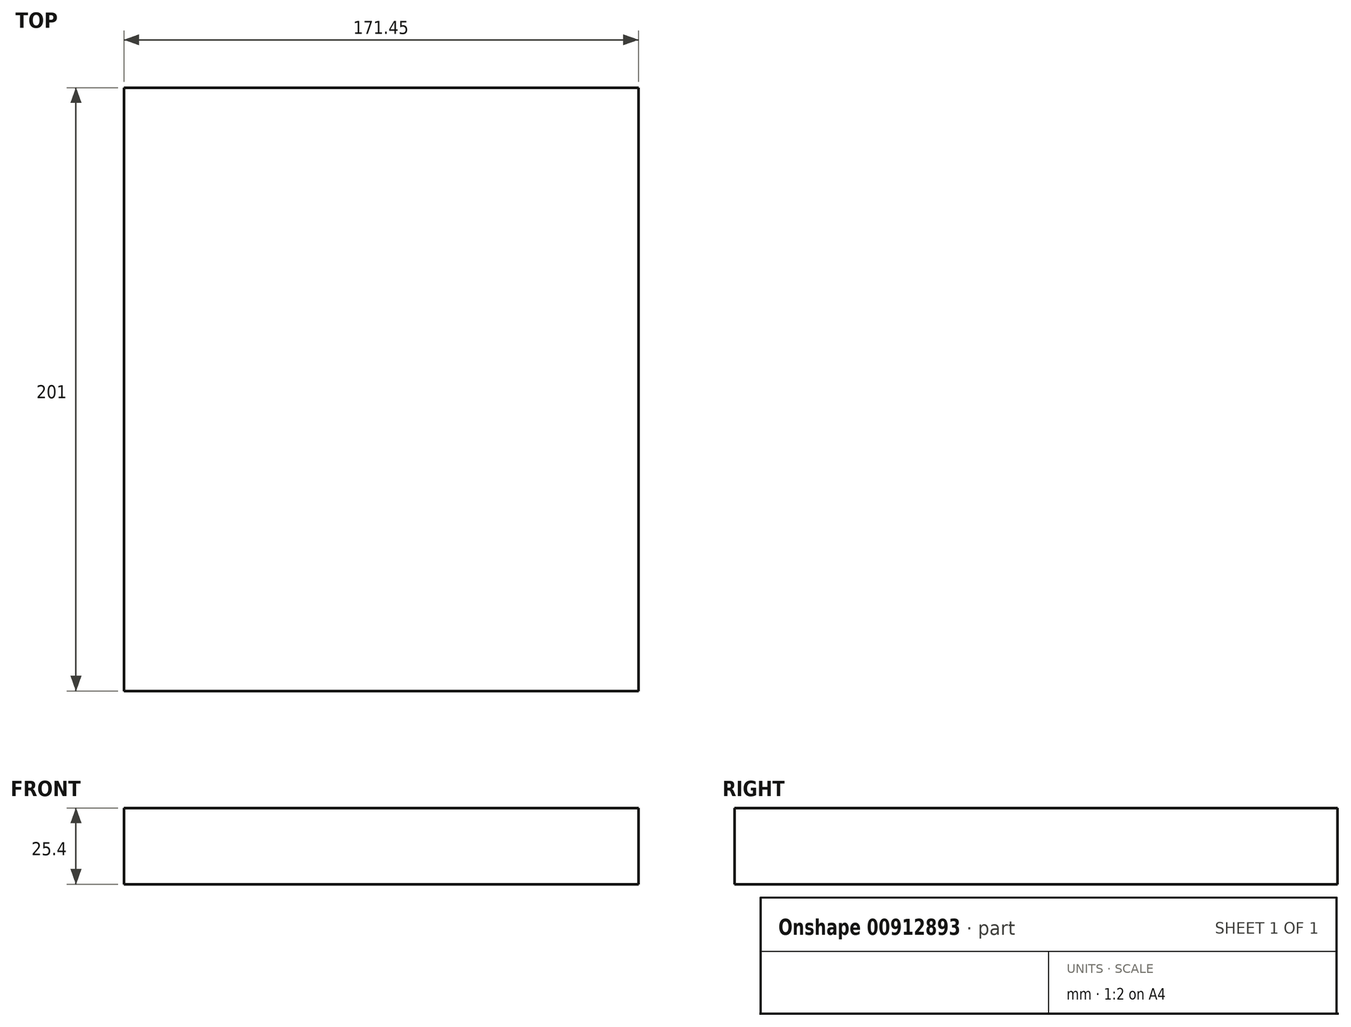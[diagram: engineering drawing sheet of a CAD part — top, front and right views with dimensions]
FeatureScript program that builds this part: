
annotation { "Feature Type Name" : "Feature", "Feature Type Description" : "" }
export const myFeature = defineFeature(function(context is Context, id is Id, definition is map)
    precondition{}
    {
        {
            var Q0;
            Q0=qCreatedBy(makeId("Top.planeOp"),FACE);
            var sketch = newSketch(context, id + "F0", { "sketchPlane" : qUnion([Q0])});
            skLineSegment(sketch, "E0.bottom", {"start": v(-102.54, 134.47) * mm, "end": v(68.91, 134.47) * mm});
            skLineSegment(sketch, "E0.top", {"start": v(-102.54, -66.53) * mm, "end": v(68.91, -66.53) * mm});
            skLineSegment(sketch, "E0.left", {"start": v(-102.54, 134.47) * mm, "end": v(-102.54, -66.53) * mm});
            skLineSegment(sketch, "E0.right", {"start": v(68.91, 134.47) * mm, "end": v(68.91, -66.53) * mm});
            skSolve(sketch);
        }
        {
            var Q0;
            Q0=makeQuery(id+"F0.imprint","IMPRINT",FACE,{"disambiguationData":[TD([[makeQuery(id+"F0.imprint","IMPRINT",EDGE,{"derivedFrom":sQuery(id+"F0.wireOp",EDGE,"E0.bottom")}),-1.0]])]});
            extrude(context, id + "F1", {"entities" : qUnion([Q0]), "depth" : 25.4 * mm, "offsetDistance" : 25.4 * mm});
        }
    });
